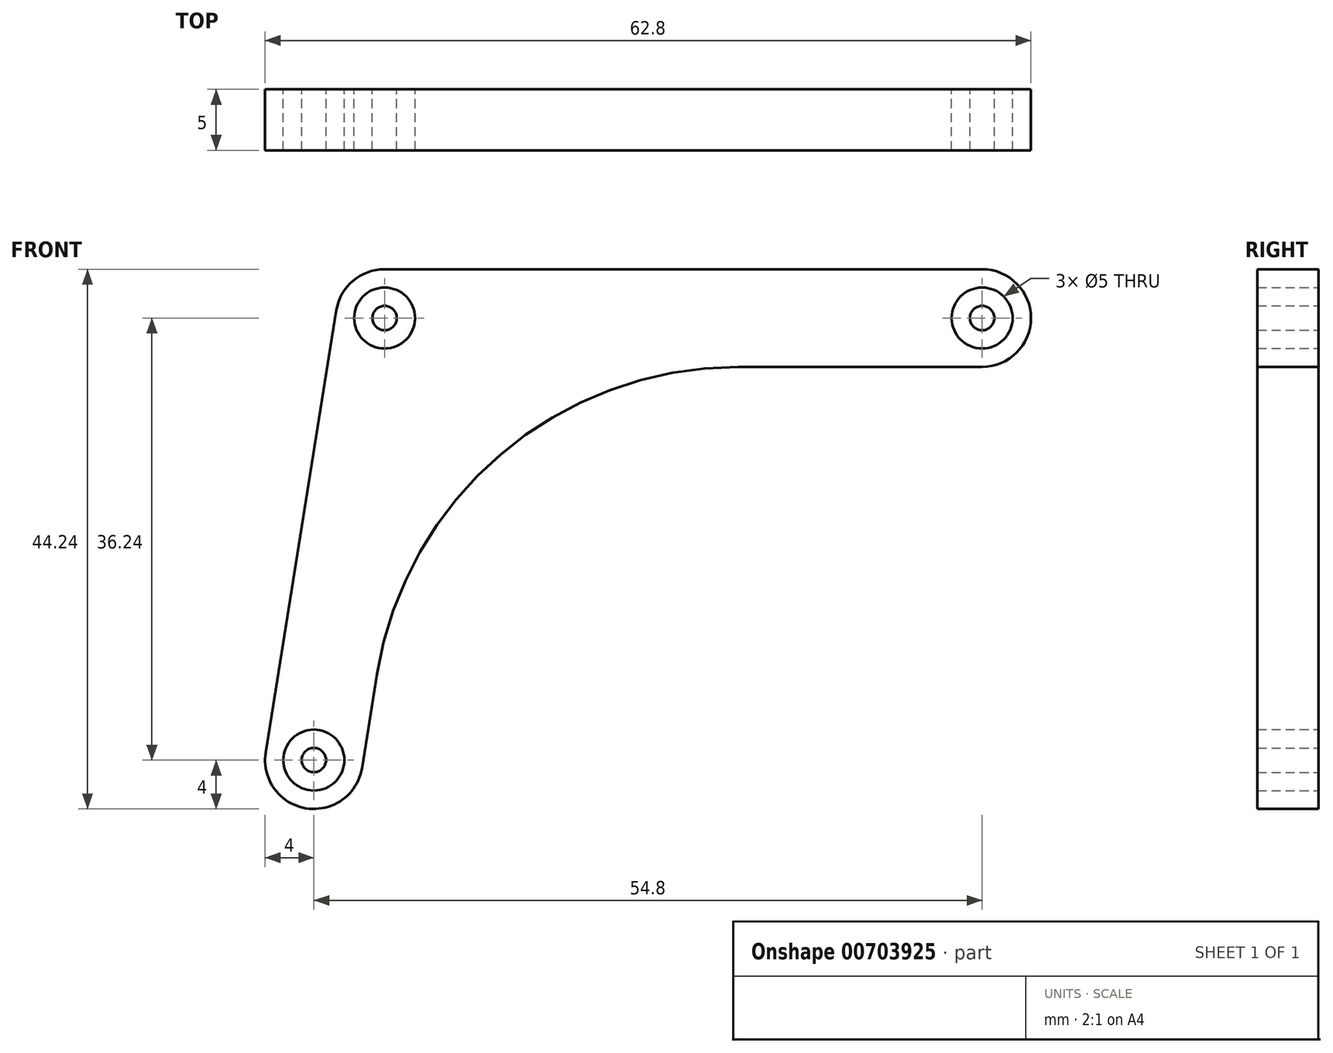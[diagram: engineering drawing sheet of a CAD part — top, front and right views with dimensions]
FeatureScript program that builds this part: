
annotation { "Feature Type Name" : "Feature", "Feature Type Description" : "" }
export const myFeature = defineFeature(function(context is Context, id is Id, definition is map)
    precondition{}
    {
        {
            var Q0;
            Q0=qCreatedBy(makeId("Front.planeOp"),FACE);
            var sketch = newSketch(context, id + "F0", { "sketchPlane" : qUnion([Q0])});
            skArc(sketch, "E0", {"start": v(0, 4) * mm, "mid": v(-2.6, 3.04) * mm, "end": v(-3.95, 0.63) * mm});
            skCircle(sketch, "E1", {"center": v(0, 0) * mm, "radius": 2.5 * mm});
            skArc(sketch, "E2", {"start": v(-9.75, -35.6) * mm, "mid": v(-6.43, -40.19) * mm, "end": v(-1.85, -36.87) * mm});
            skLineSegment(sketch, "E3", {"start": v(-3.95, 0.63) * mm, "end": v(-9.75, -35.6) * mm});
            skArc(sketch, "E4", {"start": v(49, -4) * mm, "mid": v(53, 0) * mm, "end": v(49, 4) * mm});
            skLineSegment(sketch, "E5", {"start": v(0, 4) * mm, "end": v(49, 4) * mm});
            skLineSegment(sketch, "E6.0", {"start": v(29, -4) * mm, "end": v(49, -4) * mm});
            skLineSegment(sketch, "E7.0", {"start": v(-0.63, -29.26) * mm, "end": v(-1.85, -36.87) * mm});
            skPoint(sketch, "E8.visualSharp", {"position": v(3.41, -4) * mm});
            skArc(sketch, "E8.filletArc", {"start": v(29, -4) * mm, "mid": v(9.53, -11.17) * mm, "end": v(-0.63, -29.26) * mm});
            skCircle(sketch, "E9", {"center": v(-5.8, -36.24) * mm, "radius": 2.5 * mm});
            skCircle(sketch, "E10", {"center": v(49, 0) * mm, "radius": 2.5 * mm});
            skSolve(sketch);
        }
        {
            var Q0;
            Q0=makeQuery(id+"F0.imprint","IMPRINT",FACE,{"disambiguationData":[TD([[makeQuery(id+"F0.imprint","IMPRINT",EDGE,{"derivedFrom":sQuery(id+"F0.wireOp",EDGE,"E0")}),1.0]])]});
            extrude(context, id + "F1", {"entities" : qUnion([Q0]), "depth" : 5 * mm, "offsetDistance" : 25 * mm});
        }
        {
            var Q0;
            Q0=qCreatedBy(makeId("Front.planeOp"),FACE);
            var sketch = newSketch(context, id + "F2", { "sketchPlane" : qUnion([Q0])});
            skCircle(sketch, "E11.0", {"center": v(0, 0) * mm, "radius": 2.5 * mm, "construction": true});
            skCircle(sketch, "E11.1", {"center": v(49, 0) * mm, "radius": 2.5 * mm, "construction": true});
            skCircle(sketch, "E11.2", {"center": v(-5.8, -36.24) * mm, "radius": 2.5 * mm, "construction": true});
            skCircle(sketch, "E12", {"center": v(0, 0) * mm, "radius": 1 * mm});
            skCircle(sketch, "E13", {"center": v(-5.8, -36.24) * mm, "radius": 1 * mm});
            skCircle(sketch, "E14", {"center": v(49, 0) * mm, "radius": 1 * mm});
            skSolve(sketch);
        }
        {
            var Q0;
            Q0=makeQuery(id+"F2.imprint","IMPRINT",FACE,{"disambiguationData":[TD([[makeQuery(id+"F2.imprint","IMPRINT",EDGE,{"derivedFrom":sQuery(id+"F2.wireOp",EDGE,"E12")}),1.0]])]});
            var Q1;
            Q1=makeQuery(id+"F2.imprint","IMPRINT",FACE,{"disambiguationData":[TD([[makeQuery(id+"F2.imprint","IMPRINT",EDGE,{"derivedFrom":sQuery(id+"F2.wireOp",EDGE,"E13")}),1.0]])]});
            var Q2;
            Q2=makeQuery(id+"F2.imprint","IMPRINT",FACE,{"disambiguationData":[TD([[makeQuery(id+"F2.imprint","IMPRINT",EDGE,{"derivedFrom":sQuery(id+"F2.wireOp",EDGE,"E14")}),1.0]])]});
            extrude(context, id + "F3", {"entities" : qUnion([Q0, Q1, Q2]), "depth" : 5 * mm, "offsetDistance" : 25 * mm});
        }
    });
